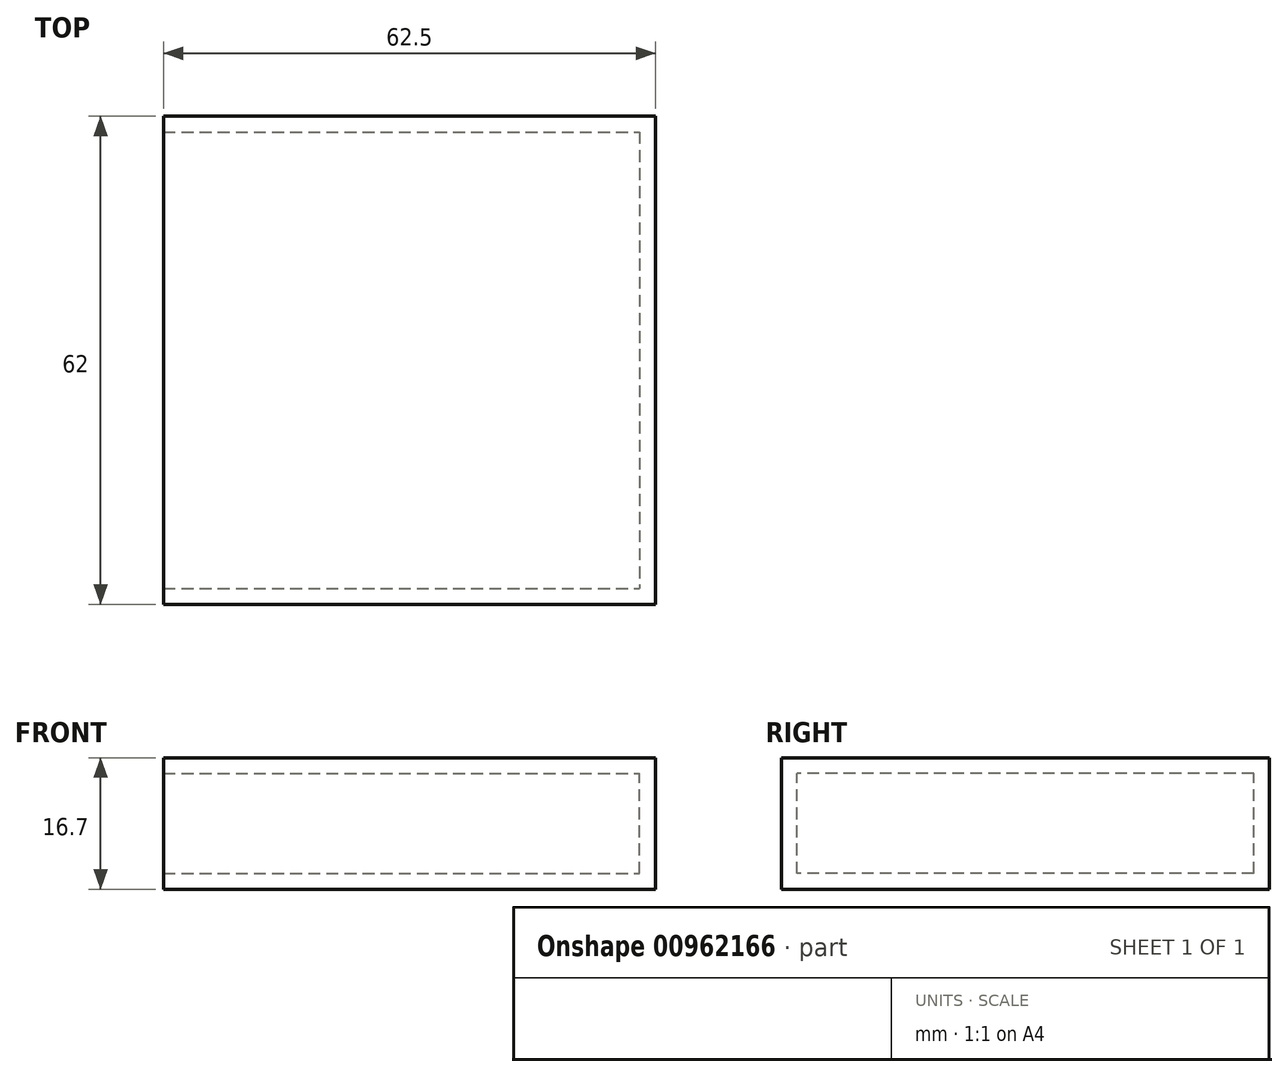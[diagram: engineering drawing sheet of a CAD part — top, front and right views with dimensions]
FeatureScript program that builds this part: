
annotation { "Feature Type Name" : "Feature", "Feature Type Description" : "" }
export const myFeature = defineFeature(function(context is Context, id is Id, definition is map)
    precondition{}
    {
        {
            var Q0;
            Q0=qCreatedBy(makeId("Top.planeOp"),FACE);
            var sketch = newSketch(context, id + "F0", { "sketchPlane" : qUnion([Q0])});
            skLineSegment(sketch, "E0.bottom", {"start": v(0, 62) * mm, "end": v(55, 62) * mm});
            skLineSegment(sketch, "E0.top", {"start": v(0, 0) * mm, "end": v(55, 0) * mm});
            skLineSegment(sketch, "E0.right", {"start": v(55, 62) * mm, "end": v(55, 0) * mm});
            skLineSegment(sketch, "E1.left", {"start": v(0, 62) * mm, "end": v(0, -13) * mm});
            skLineSegment(sketch, "E2.bottom", {"start": v(0, 62) * mm, "end": v(-7.5, 62) * mm});
            skLineSegment(sketch, "E2.top", {"start": v(0, 0) * mm, "end": v(-7.5, 0) * mm});
            skLineSegment(sketch, "E2.left", {"start": v(0, 62) * mm, "end": v(0, 0) * mm});
            skLineSegment(sketch, "E2.right", {"start": v(-7.5, 62) * mm, "end": v(-7.5, 0) * mm});
            skSolve(sketch);
        }
        {
            var Q0;
            Q0 = qSketchRegion(id + "F0", true);
            extrude(context, id + "F1", {"entities" : qUnion([Q0]), "depth" : -16.7 * mm, "offsetDistance" : 25.4 * mm});
        }
        {
            var Q0;
            Q0=makeQuery(id+"F1.opExtrude","SWEPT_FACE",FACE,{"disambiguationData":[OSD([sQuery(id+"F0.wireOp",EDGE,"E2.right")])]});
            shell(context, id + "F2", {"entities" : qUnion([Q0]), "thickness" : 2 * mm});
        }
    });
